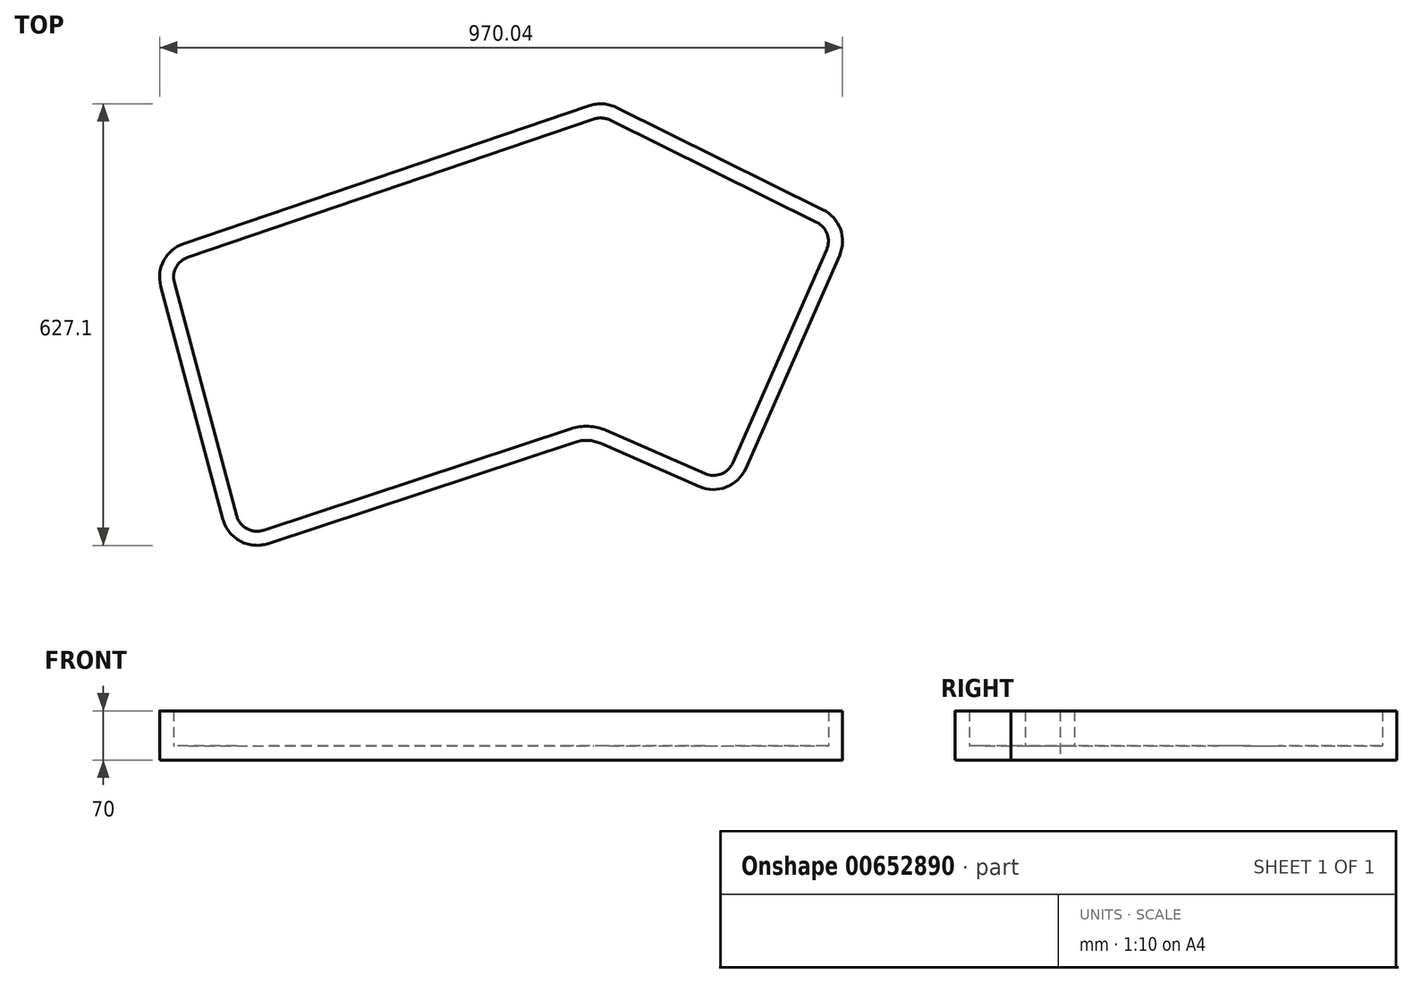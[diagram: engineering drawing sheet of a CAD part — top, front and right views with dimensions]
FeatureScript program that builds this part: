
annotation { "Feature Type Name" : "Feature", "Feature Type Description" : "" }
export const myFeature = defineFeature(function(context is Context, id is Id, definition is map)
    precondition{}
    {
        {
            var Q0;
            Q0=qCreatedBy(makeId("Top.planeOp"),FACE);
            var sketch = newSketch(context, id + "F0", { "sketchPlane" : qUnion([Q0])});
            skLineSegment(sketch, "E0", {"start": v(-450.1, 122.58) * mm, "end": v(126.41, 318.75) * mm});
            skLineSegment(sketch, "E1", {"start": v(164.68, 316.23) * mm, "end": v(458.2, 171.12) * mm});
            skLineSegment(sketch, "E2", {"start": v(106.35, -159.1) * mm, "end": v(-329.97, -303.17) * mm});
            skLineSegment(sketch, "E3", {"start": v(-393.96, -268.59) * mm, "end": v(-482.3, 62.35) * mm});
            skLineSegment(sketch, "E4", {"start": v(481.8, 106.14) * mm, "end": v(348.5, -196.48) * mm});
            skLineSegment(sketch, "E5", {"start": v(282.75, -222.15) * mm, "end": v(142.02, -160.74) * mm});
            skPoint(sketch, "E6.visualSharp", {"position": v(-380.29, -319.78) * mm});
            skArc(sketch, "E6.filletArc", {"start": v(-393.96, -268.59) * mm, "mid": v(-369.42, -299.68) * mm, "end": v(-329.97, -303.17) * mm});
            skPoint(sketch, "E7.visualSharp", {"position": v(-494.36, 107.52) * mm});
            skArc(sketch, "E7.filletArc", {"start": v(-450.1, 122.58) * mm, "mid": v(-478.1, 98.82) * mm, "end": v(-482.3, 62.35) * mm});
            skPoint(sketch, "E8.visualSharp", {"position": v(124.5, -153.1) * mm});
            skArc(sketch, "E8.filletArc", {"start": v(142.02, -160.74) * mm, "mid": v(124.33, -156.63) * mm, "end": v(106.35, -159.1) * mm});
            skPoint(sketch, "E9.visualSharp", {"position": v(328.42, -242.08) * mm});
            skArc(sketch, "E9.filletArc", {"start": v(282.75, -222.15) * mm, "mid": v(320.93, -222.9) * mm, "end": v(348.5, -196.48) * mm});
            skPoint(sketch, "E10.visualSharp", {"position": v(501.08, 149.92) * mm});
            skArc(sketch, "E10.filletArc", {"start": v(481.8, 106.14) * mm, "mid": v(483.03, 143.37) * mm, "end": v(458.2, 171.12) * mm});
            skPoint(sketch, "E11.visualSharp", {"position": v(146.07, 325.44) * mm});
            skArc(sketch, "E11.filletArc", {"start": v(164.68, 316.23) * mm, "mid": v(145.8, 321.3) * mm, "end": v(126.41, 318.75) * mm});
            skLineSegment(sketch, "E12.bottom", {"start": v(769.44, -500) * mm, "end": v(-769.44, -500) * mm});
            skLineSegment(sketch, "E12.top", {"start": v(769.44, 500) * mm, "end": v(-769.44, 500) * mm});
            skLineSegment(sketch, "E12.left", {"start": v(769.44, -500) * mm, "end": v(769.44, 500) * mm});
            skLineSegment(sketch, "E12.right", {"start": v(-769.44, -500) * mm, "end": v(-769.44, 500) * mm});
            skPoint(sketch, "E12.middle", {"position": v(0, 0) * mm});
            skSolve(sketch);
        }
        {
            var Q0;
            Q0=makeQuery(id+"F0.imprint","IMPRINT",FACE,{"disambiguationData":[TD([[makeQuery(id+"F0.imprint","IMPRINT",EDGE,{"derivedFrom":sQuery(id+"F0.wireOp",EDGE,"E0")}),-1.0]])]});
            extrude(context, id + "F1", {"entities" : qUnion([Q0]), "depth" : 20 * mm, "offsetDistance" : 25 * mm});
        }
        {
            var Q0;
            Q0=makeQuery(id+"F1.opExtrude","CAP_FACE",FACE,{"disambiguationData":[OSD([sQuery(id+"F0.wireOp",EDGE,"E0"),sQuery(id+"F0.wireOp",EDGE,"E1"),sQuery(id+"F0.wireOp",EDGE,"E2"),sQuery(id+"F0.wireOp",EDGE,"E3"),sQuery(id+"F0.wireOp",EDGE,"E4"),sQuery(id+"F0.wireOp",EDGE,"E5"),sQuery(id+"F0.wireOp",EDGE,"E6.filletArc"),sQuery(id+"F0.wireOp",EDGE,"E7.filletArc"),sQuery(id+"F0.wireOp",EDGE,"E8.filletArc"),sQuery(id+"F0.wireOp",EDGE,"E9.filletArc"),sQuery(id+"F0.wireOp",EDGE,"E10.filletArc"),sQuery(id+"F0.wireOp",EDGE,"E11.filletArc")])],"isStart":false});
            extrude(context, id + "F2", {"entities" : qUnion([Q0]), "operationType" : NewBodyOperationType.ADD, "depth" : 50 * mm, "offsetDistance" : 25 * mm});
        }
        {
            var Q0;
            Q0=makeQuery(id+"F2.opExtrude","CAP_FACE",FACE,{"disambiguationData":[OSD([sQuery(id+"F0.wireOp",EDGE,"E0"),sQuery(id+"F0.wireOp",EDGE,"E1"),sQuery(id+"F0.wireOp",EDGE,"E2"),sQuery(id+"F0.wireOp",EDGE,"E3"),sQuery(id+"F0.wireOp",EDGE,"E4"),sQuery(id+"F0.wireOp",EDGE,"E5"),sQuery(id+"F0.wireOp",EDGE,"E6.filletArc"),sQuery(id+"F0.wireOp",EDGE,"E7.filletArc"),sQuery(id+"F0.wireOp",EDGE,"E8.filletArc"),sQuery(id+"F0.wireOp",EDGE,"E9.filletArc"),sQuery(id+"F0.wireOp",EDGE,"E10.filletArc"),sQuery(id+"F0.wireOp",EDGE,"E11.filletArc")])],"isStart":false});
            shell(context, id + "F3", {"entities" : qUnion([Q0]), "thickness" : 20 * mm});
        }
    });
